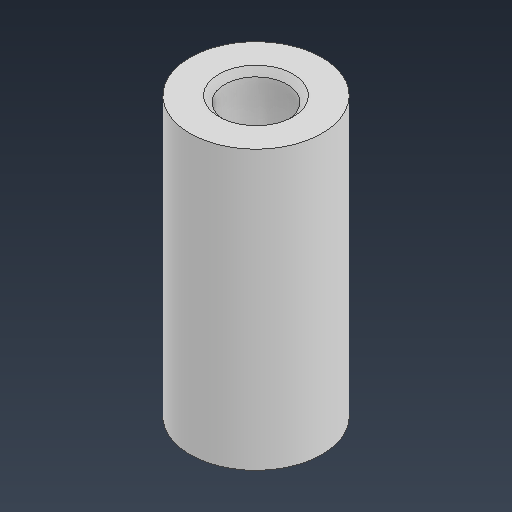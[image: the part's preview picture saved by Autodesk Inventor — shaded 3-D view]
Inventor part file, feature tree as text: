
AUTODESK INVENTOR PART (.ipt)
format: ipt  version: 2025.3 (Build 293356000, 356)  size: 103,936 bytes
history: native  units: mm
features: sketch x3, hole x2, extrude x1
ambient origin geometry x8: Origin, YZ Plane, XZ Plane, XY Plane, X Axis, Y Axis, Z Axis, Center Point
bodies: Solid1 (feature_tree)
feature tree (6):
  extrude  "Extrusion1"  Depth=16.88mm TaperAngle=0.0deg
  sketch  "Sketch2"  dims[d3=3.78mm d4=6.0mm d5=4.5mm d6=2.0mm d7=90.0deg d8=6.0mm d9=0.0mm]
  hole  "Hole1"  [1 undecoded]
  hole  "Hole2"  [1 undecoded]
  sketch  "Sketch1"  dims[d0=8.0mm d1=16.88mm d2=0.0mm]
  sketch  "Sketch3"  dims[d10=3.78mm d11=6.0mm d12=4.5mm d13=2.0mm d14=90.0deg d15=6.0mm d16=0.0mm]
note: 2 required parameter values undecoded (feature->parameter linkage not recoverable at this tier; creation-order binding heuristic only, values carry confidence <= 0.55)
